# Revit family: logis_universal_shaving_mirror_with_led_light_73560000
name_source: partatom
category: Generic Models
revit_build: Autodesk Revit 2015 (Build: 20140903_1530(x64)
units: mm (PartAtom-declared; Revit-internal decimal feet)

## types (1)
- Chrome 000
    BOSUseNativeGeometries = 1
    Brand url = http://www.hansgrohe-int.com
    Default Elevation = 4' - 0"
    Design country = Germany
    EAN code = https://4059625136584
    Edition number = 1
    IFC Classification = Furniture
    Installation instructions = https://pro.hansgrohe-int.com
    Manufacturer country = Germany
    Manufacturer name = hansgrohe
    Masterformat 2014 Code = 08 83 00
    Masterformat 2014 Description = Mirrors
    Material main = Chrome
    NBS Reference Code = 45-55-06
    NBS Reference Description = Bathroom Mirrors
    Nominal height = 0
    Nominal width = 0
    OmniClass Code = 23-21 37 13 15
    OmniClass Description = Mirrors
    Product Guid = 7f824e72-8aaa-48aa-bad0-ec6972f20d81
    Product SKU = 73560000
    Product data url = https://bimobject.com
    Product family = Logis Universal
    Product group = Accessories
    Product name = Logis Universal Shaving mirror with LED light 73560000
    Product url = https://pro.hansgrohe-int.com
    QR code = http://bimobject.com
    Technical description = https://pro.hansgrohe-int.com
    UNSPSC Code = 56
    Uniclass 1.4 Code = L8732
    Uniclass 1.4 Description = Mirrors
    Uniclass 2.0 Code = PR-45-55-06
    Uniclass 2.0 Description = Bathroom Mirrors
    Uniclass 2015 Code = Pr_25_71_53_06
    Uniclass 2015 Name = Bathroom mirrors
    Uniformat II Code = E20
    Uniformat II Description = FURNISHINGS
    Weight Net (Kg) = 0

## geometry (parser evidence)
native form markers: Sweep x2
no freeform markers — native parametric forms only
